# Revit family: 2059212 Lighting Fixture_Sylvania_Ascent 100 Deco(160)-Very High Output_Ceiling Recessed
name_source: partatom
category: Lighting Fixtures
revit_build: Autodesk Revit 2017 (Build: 20190507_1515(x64)
units: mm (PartAtom-declared; Revit-internal decimal feet)

## family parameters
Cut with Voids When Loaded = No
Host = Face
Light Source = Yes
OmniClass Number = 23.80.70.11.17
OmniClass Title = Specialized Lighting by Location or Use
Part Type = Normal
Room Calculation Point = No
Round Connector Dimension = Use Diameter
Shared = No

## types (1)
- Asct100 Deco VHO 3K STDEMG 160
    Aperture = 160 mm  [stored 0.524934 ft]
    Apparent Load = 25 VA
    Assembly Code = D5020200
    Body Material = Aluminum_Sylvania_Ascent_White
    Catalog Number = 2059212 Asct100 Deco VHO 3K STDEMG 160
    Color Filter = 16777215
    Cutout Diameter = 178 mm  [stored 0.58399 ft]
    Default Elevation = 0 mm  [stored 0 ft]
    Description = Direct LED retro fit for original LED 100 Deco (160) single CFL lamp offering Matching lumen levels and improved light distribution of original LED 100 CFL lamp equivalents Typically half the power consumption compared to CFL Up to 112lm/W 160mm aperture Decorative reflector accepts snap fit polycarbonate accessories from existing LED 100 Deco 160 offering New kometa accessory ring creates a diffused indirect halo of light onto the ceiling for decorative effect HE, HO and VHO versions equivalent of single 1 x 18W, 1 x 32W, 1 x 42W Additional VVHO versions which offer the performance circa 2 x 32W equivalent
    Diameter = 189 mm  [stored 0.620079 ft]
    Diffuser Material = Polycarbonate_Sylvania_Ascent_Clear
    Diffuser Radius = 76 mm  [stored 0.249344 ft]
    Dimming Lamp Color Temperature Shift = <None>
    Drive Current = 1000mA
    Emit Shape Visible in Rendering = No
    Emit from Circle Diameter = 152 mm  [stored 0.498688 ft]
    Glow Wire Test = 850 °C
    Height = 94 mm  [stored 0.308399 ft]
    IK Rating = IK02
    IP Rating = IP44
    Lamp = Integrated LED
    Life = 50 000h
    Manufacturer = Feilo-Sylvania Group
    Model = Asct100 Deco VHO 3K STDEMG 160
    Photometric Web File = 2059212_Asct100DecoVHO3KSTDEMG160-190134.ies
    Product Family = Ascent 100 Deco (160) - Very High Output
    Product Page URL = https://www.sylvania-lighting.com
    Radius = 94.5 mm  [stored 0.310039 ft]
    Reflector Material = Aluminium_Sylvania_Ascent_Silver
    Reflector Radius = 80 mm  [stored 0.262467 ft]
    Tilt Angle = -90°
    URL = https://www.sylvania-lighting.com
    Voltage = 240 V
    Voltage Comments = UNV (Universal Voltage; 220-240 Volt)

note: [stored X ft] marks values corroborated as IEEE doubles in the binary element streams (Revit-internal decimal feet)

## geometry (parser evidence)
native form markers: Sweep x3
no freeform markers — native parametric forms only
